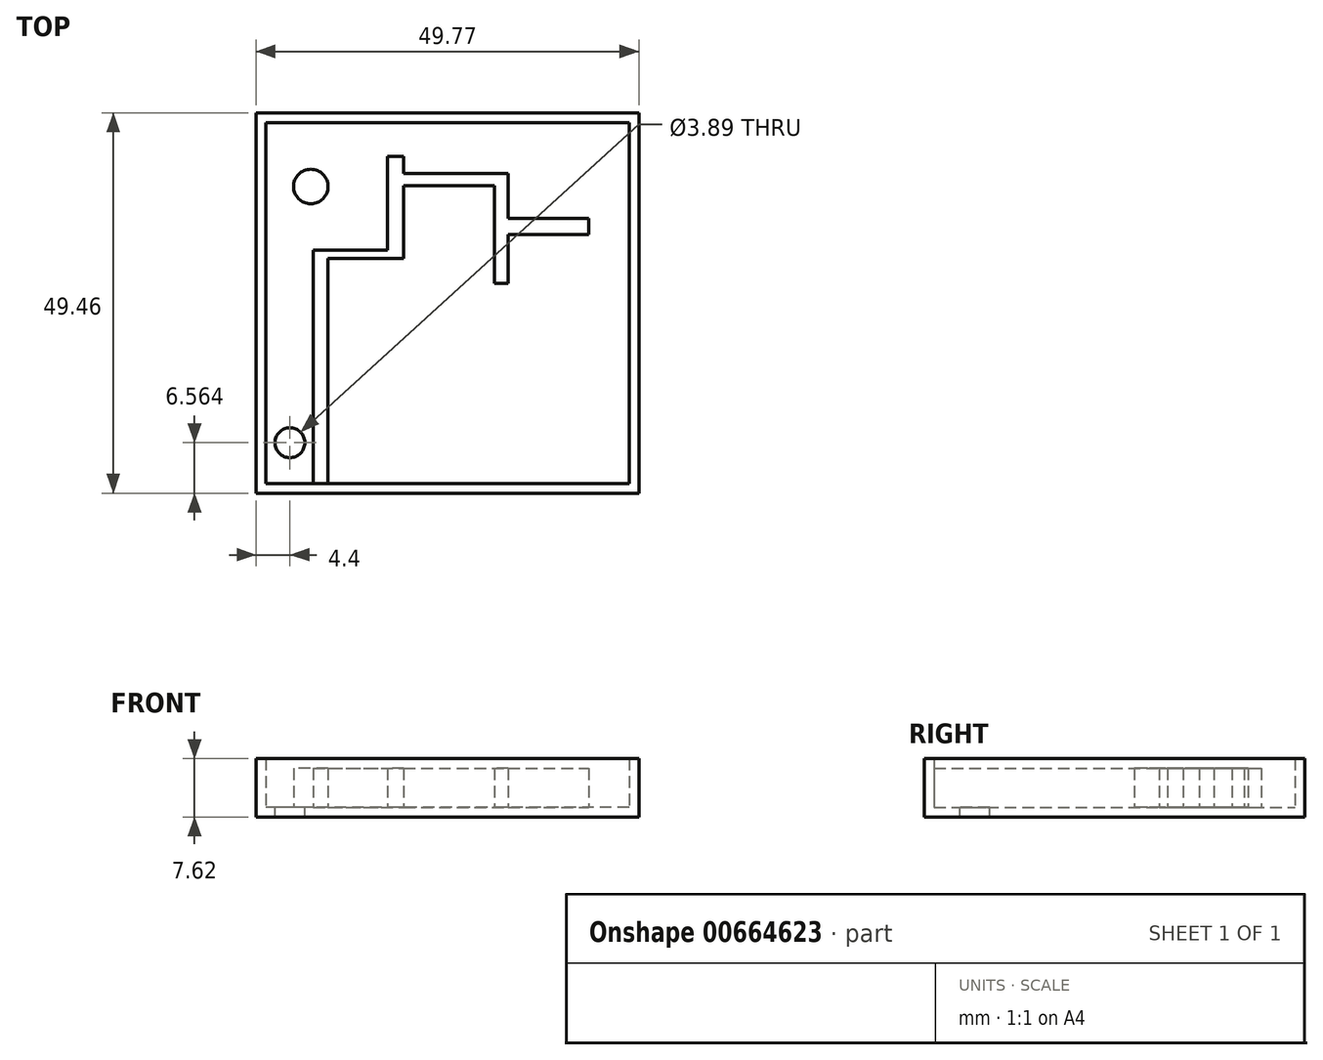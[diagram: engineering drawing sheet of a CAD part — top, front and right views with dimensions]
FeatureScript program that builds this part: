
annotation { "Feature Type Name" : "Feature", "Feature Type Description" : "" }
export const myFeature = defineFeature(function(context is Context, id is Id, definition is map)
    precondition{}
    {
        {
            var Q0;
            Q0=qCreatedBy(makeId("Top.planeOp"),FACE);
            var sketch = newSketch(context, id + "F0", { "sketchPlane" : qUnion([Q0])});
            skLineSegment(sketch, "E0.bottom", {"start": v(0, 0) * mm, "end": v(-49.77, 0) * mm});
            skLineSegment(sketch, "E0.top", {"start": v(0, 49.46) * mm, "end": v(-49.77, 49.46) * mm});
            skLineSegment(sketch, "E0.left", {"start": v(0, 0) * mm, "end": v(0, 49.46) * mm});
            skLineSegment(sketch, "E0.right", {"start": v(-49.77, 0) * mm, "end": v(-49.77, 49.46) * mm});
            skSolve(sketch);
        }
        {
            var Q0;
            Q0 = qSketchRegion(id + "F0", true);
            extrude(context, id + "F1", {"entities" : qUnion([Q0]), "depth" : 7.62 * mm, "offsetDistance" : 25.4 * mm});
        }
        {
            var Q0;
            Q0=makeQuery(id+"F1.opExtrude","CAP_FACE",FACE,{"disambiguationData":[OSD([sQuery(id+"F0.wireOp",EDGE,"E0.bottom"),sQuery(id+"F0.wireOp",EDGE,"E0.top"),sQuery(id+"F0.wireOp",EDGE,"E0.left"),sQuery(id+"F0.wireOp",EDGE,"E0.right")])],"isStart":false});
            shell(context, id + "F2", {"entities" : qUnion([Q0]), "thickness" : 1.27 * mm});
        }
        {
            var Q0;
            Q0=makeQuery(id+"F2.opShell","OFFSET_FACE",FACE,{"disambiguationData":[OSD([sQuery(id+"F0.wireOp",EDGE,"E0.bottom"),sQuery(id+"F0.wireOp",EDGE,"E0.top"),sQuery(id+"F0.wireOp",EDGE,"E0.left"),sQuery(id+"F0.wireOp",EDGE,"E0.right")])]});
            var sketch = newSketch(context, id + "F3", { "sketchPlane" : qUnion([Q0])});
            skLineSegment(sketch, "E1.bottom", {"start": v(-48.5, 1.27) * mm, "end": v(-44.25, 1.27) * mm});
            skLineSegment(sketch, "E1.top", {"start": v(-48.5, 1.27) * mm, "end": v(-44.25, 1.27) * mm});
            skLineSegment(sketch, "E1.left", {"start": v(-48.5, 1.27) * mm, "end": v(-48.5, 1.27) * mm});
            skLineSegment(sketch, "E1.right", {"start": v(-44.25, 1.27) * mm, "end": v(-44.25, 1.27) * mm});
            skLineSegment(sketch, "E2.bottom", {"start": v(-42.3, 1.27) * mm, "end": v(-40.4, 1.27) * mm});
            skLineSegment(sketch, "E2.top", {"start": v(-42.3, 31.62) * mm, "end": v(-40.4, 31.62) * mm});
            skLineSegment(sketch, "E2.left", {"start": v(-42.3, 1.27) * mm, "end": v(-42.3, 31.62) * mm});
            skLineSegment(sketch, "E2.right", {"start": v(-40.4, 1.27) * mm, "end": v(-40.4, 31.62) * mm});
            skLineSegment(sketch, "E3.bottom", {"start": v(-40.4, 30.52) * mm, "end": v(-30.57, 30.52) * mm});
            skLineSegment(sketch, "E3.top", {"start": v(-40.4, 31.62) * mm, "end": v(-30.57, 31.62) * mm});
            skLineSegment(sketch, "E3.left", {"start": v(-40.4, 30.52) * mm, "end": v(-40.4, 31.62) * mm});
            skLineSegment(sketch, "E3.right", {"start": v(-30.57, 30.52) * mm, "end": v(-30.57, 31.62) * mm});
            skLineSegment(sketch, "E4.bottom", {"start": v(-30.57, 31.62) * mm, "end": v(-32.69, 31.62) * mm});
            skLineSegment(sketch, "E4.top", {"start": v(-30.57, 43.8) * mm, "end": v(-32.69, 43.8) * mm});
            skLineSegment(sketch, "E4.left", {"start": v(-30.57, 31.62) * mm, "end": v(-30.57, 43.8) * mm});
            skLineSegment(sketch, "E4.right", {"start": v(-32.69, 31.62) * mm, "end": v(-32.69, 43.8) * mm});
            skCircle(sketch, "E5", {"center": v(-42.65, 39.88) * mm, "radius": 2.24 * mm});
            skLineSegment(sketch, "E6.bottom", {"start": v(-30.57, 41.6) * mm, "end": v(-16.99, 41.6) * mm});
            skLineSegment(sketch, "E6.top", {"start": v(-30.57, 39.98) * mm, "end": v(-16.99, 39.98) * mm});
            skLineSegment(sketch, "E6.left", {"start": v(-30.57, 41.6) * mm, "end": v(-30.57, 39.98) * mm});
            skLineSegment(sketch, "E6.right", {"start": v(-16.99, 41.6) * mm, "end": v(-16.99, 39.98) * mm});
            skLineSegment(sketch, "E7.bottom", {"start": v(-16.99, 39.98) * mm, "end": v(-18.8, 39.98) * mm});
            skLineSegment(sketch, "E7.top", {"start": v(-16.99, 27.3) * mm, "end": v(-18.8, 27.3) * mm});
            skLineSegment(sketch, "E7.left", {"start": v(-16.99, 39.98) * mm, "end": v(-16.99, 27.3) * mm});
            skLineSegment(sketch, "E7.right", {"start": v(-18.8, 39.98) * mm, "end": v(-18.8, 27.3) * mm});
            skPoint(sketch, "E8.oppositeSnap0", {"position": v(-16.99, 33.64) * mm});
            skLineSegment(sketch, "E8.bottom", {"start": v(-16.99, 35.75) * mm, "end": v(-6.52, 35.75) * mm});
            skLineSegment(sketch, "E8.top", {"start": v(-16.99, 33.64) * mm, "end": v(-6.52, 33.64) * mm});
            skLineSegment(sketch, "E8.left", {"start": v(-16.99, 35.75) * mm, "end": v(-16.99, 33.64) * mm});
            skLineSegment(sketch, "E8.right", {"start": v(-6.52, 35.75) * mm, "end": v(-6.52, 33.64) * mm});
            skSolve(sketch);
        }
        {
            var Q0;
            Q0=makeQuery(id+"F3.imprint","IMPRINT",FACE,{"disambiguationData":[TD([[makeQuery(id+"F3.imprint","IMPRINT",EDGE,{"derivedFrom":sQuery(id+"F3.wireOp",EDGE,"E2.bottom")}),-1.0]])]});
            extrude(context, id + "F4", {"entities" : qUnion([Q0]), "operationType" : NewBodyOperationType.ADD, "depth" : 5.08 * mm, "offsetDistance" : 25.4 * mm});
        }
        {
            var Q0;
            Q0 = qSketchRegion(id + "F3", true);
            extrude(context, id + "F5", {"entities" : qUnion([Q0]), "operationType" : NewBodyOperationType.ADD, "depth" : 5.08 * mm, "offsetDistance" : 25.4 * mm});
        }
        {
            var Q0;
            Q0=makeQuery(id+"F2.opShell","OFFSET_FACE",FACE,{"disambiguationData":[OSD([sQuery(id+"F0.wireOp",EDGE,"E0.bottom"),sQuery(id+"F0.wireOp",EDGE,"E0.top"),sQuery(id+"F0.wireOp",EDGE,"E0.left"),sQuery(id+"F0.wireOp",EDGE,"E0.right")])]});
            var sketch = newSketch(context, id + "F6", { "sketchPlane" : qUnion([Q0])});
            skCircle(sketch, "E9", {"center": v(-45.37, 6.56) * mm, "radius": 1.94 * mm});
            skSolve(sketch);
        }
        {
            var Q0;
            Q0 = qSketchRegion(id + "F6", true);
            extrude(context, id + "F7", {"entities" : qUnion([Q0]), "operationType" : NewBodyOperationType.REMOVE, "oppositeDirection" : true, "depth" : 5.08 * mm, "offsetDistance" : 25.4 * mm});
        }
    });
